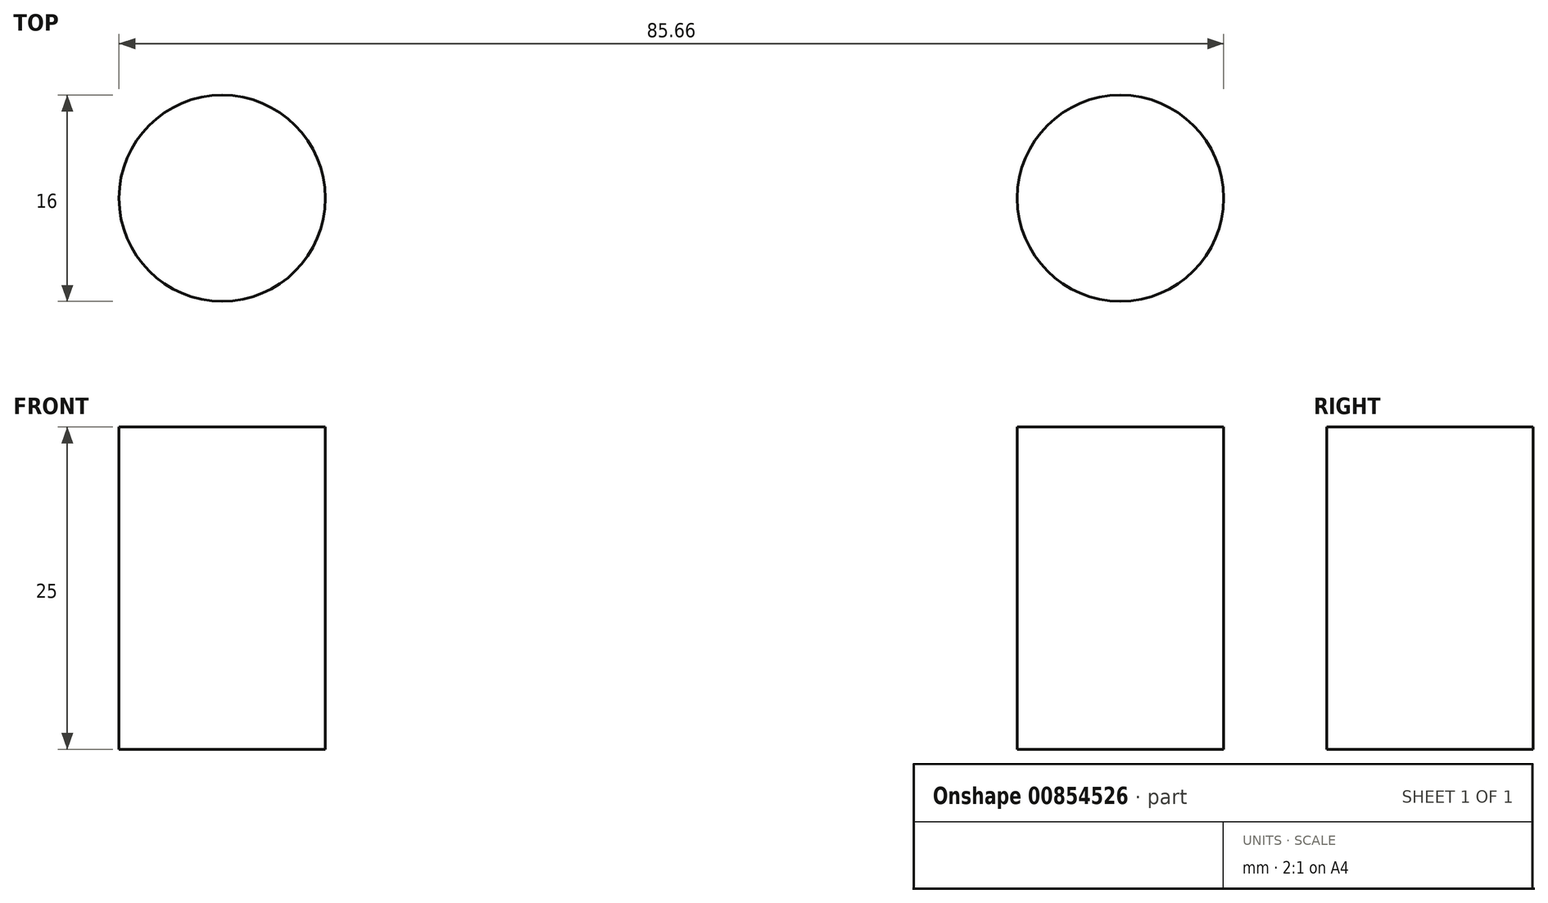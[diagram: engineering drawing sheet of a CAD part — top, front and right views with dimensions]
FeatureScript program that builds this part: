
annotation { "Feature Type Name" : "Feature", "Feature Type Description" : "" }
export const myFeature = defineFeature(function(context is Context, id is Id, definition is map)
    precondition{}
    {
        {
            var Q0;
            Q0=qCreatedBy(makeId("Top.planeOp"),FACE);
            var sketch = newSketch(context, id + "F0", { "sketchPlane" : qUnion([Q0])});
            skCircle(sketch, "E0", {"center": v(-34.83, 2.95) * mm, "radius": 8 * mm});
            skCircle(sketch, "E1", {"center": v(34.83, 2.95) * mm, "radius": 8 * mm});
            skSolve(sketch);
        }
        {
            var Q0;
            Q0=makeQuery(id+"F0.imprint","IMPRINT",FACE,{"disambiguationData":[TD([[makeQuery(id+"F0.imprint","IMPRINT",EDGE,{"derivedFrom":sQuery(id+"F0.wireOp",EDGE,"E0")}),1.0]])]});
            var Q1;
            Q1=makeQuery(id+"F0.imprint","IMPRINT",FACE,{"disambiguationData":[TD([[makeQuery(id+"F0.imprint","IMPRINT",EDGE,{"derivedFrom":sQuery(id+"F0.wireOp",EDGE,"E1")}),1.0]])]});
            extrude(context, id + "F1", {"entities" : qUnion([Q0, Q1]), "depth" : 25 * mm, "offsetDistance" : 25 * mm});
        }
    });
